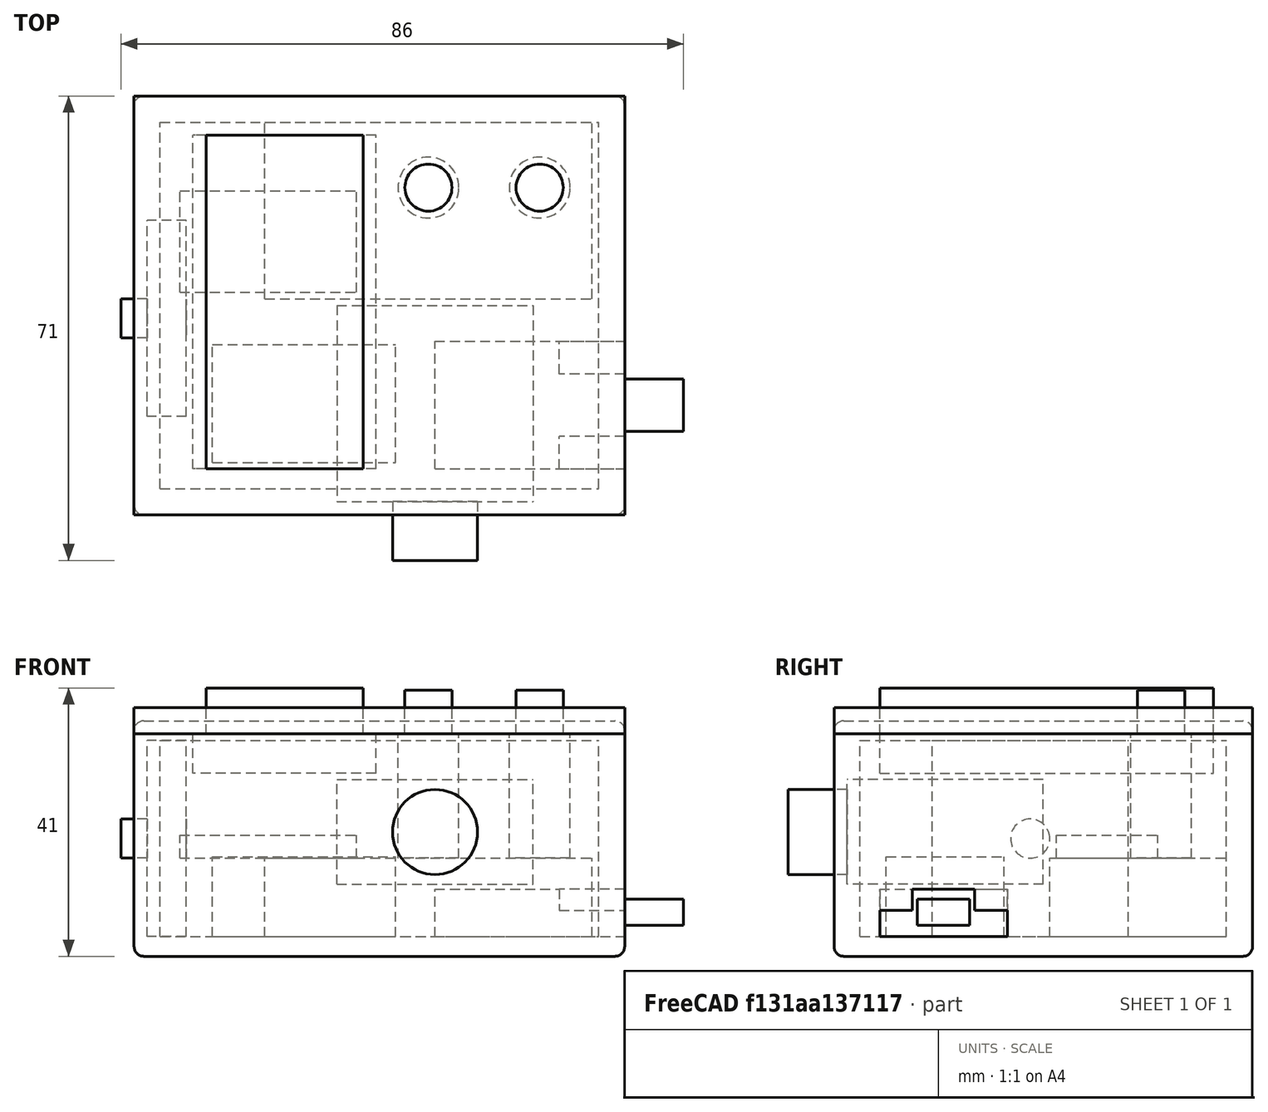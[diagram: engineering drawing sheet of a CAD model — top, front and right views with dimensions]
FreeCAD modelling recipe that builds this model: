
FCSTD DOCUMENT  (FreeCAD 0.19R)
Label: RoundTimer-partsonly
License: All rights reserved
LicenseURL: http://en.wikipedia.org/wiki/All_rights_reserved
objects: Part::Box×14, Part::Cylinder×6, Part::MultiFuse×4, Part::Fuse×2, Part::Cut×2, Part::Fillet×1
note: 29 computed .brp shape members not serialized (recipe doc carries the construction recipe); baked Part::Feature solids carry a one-line shape summary decoded from their .brp

FEATURE [Part::Box] Box  label="Cube"
  AttacherType = Attacher::AttachEngine3D
  Height = 30
  Length = 30
  Width = 16
FEATURE [Part::Cylinder] Cylinder
  Angle = 360
  AttacherType = Attacher::AttachEngine3D
  Height = 9
  Placement = pos=(15,8,30) rot=(0,0,1;0rad)
  Radius = 6.5
FEATURE [Part::Fuse] Fusion  label="Awesome switch"
  Base = -> Box
  Placement = pos=(-11,17,8) rot=(1,0,0;1.5708rad)
  Tool = -> Cylinder
FEATURE [Part::Box] Box001  label="Cube001"
  AttacherType = Attacher::AttachEngine3D
  Height = 6
  Length = 51
  Width = 28
FEATURE [Part::Box] Box002  label="Cube002"
  AttacherType = Attacher::AttachEngine3D
  Height = 7
  Length = 51
  Placement = pos=(0,2,6) rot=(0,0,1;0rad)
  Width = 24
FEATURE [Part::MultiFuse] Fusion001  label="LCD Display"
  Placement = pos=(-5,-8,25) rot=(0,0,1;1.5708rad)
  Shapes = -> [Box001,Box002]
FEATURE [Part::Box] Box003  label="Lipo Battery"
  AttacherType = Attacher::AttachEngine3D
  Height = 12
  Length = 50
  Placement = pos=(-22,18,0) rot=(0,0,1;0rad)
  Width = 27
FEATURE [Part::Cylinder] Cylinder001
  Angle = 360
  AttacherType = Attacher::AttachEngine3D
  Height = 19
  Radius = 4.65
FEATURE [Part::Cylinder] Cylinder002
  Angle = 360
  AttacherType = Attacher::AttachEngine3D
  Height = 6.7
  Placement = pos=(0,0,19) rot=(0,0,1;0rad)
  Radius = 3.6
FEATURE [Part::MultiFuse] Fusion002  label="Push Button mode/reset"
  Placement = pos=(20,35,12) rot=(1,0,0;0rad)
  Shapes = -> [Cylinder001,Cylinder002]
FEATURE [Part::Cylinder] Cylinder003
  Angle = 360
  AttacherType = Attacher::AttachEngine3D
  Height = 19
  Radius = 4.65
FEATURE [Part::Cylinder] Cylinder004
  Angle = 360
  AttacherType = Attacher::AttachEngine3D
  Height = 6.7
  Placement = pos=(0,0,19) rot=(0,0,1;0rad)
  Radius = 3.6
FEATURE [Part::MultiFuse] Fusion003  label="Push Button start/stop"
  Placement = pos=(3,35,12) rot=(1,0,0;0rad)
  Shapes = -> [Cylinder003,Cylinder004]
FEATURE [Part::Box] Box004  label="Cube003"
  AttacherType = Attacher::AttachEngine3D
  Height = 7.25
  Length = 29
  Width = 19.5
FEATURE [Part::Box] Box005  label="Cube004"
  AttacherType = Attacher::AttachEngine3D
  Height = 4
  Length = 10
  Placement = pos=(28,5.75,1.75) rot=(0,0,1;0rad)
  Width = 8
FEATURE [Part::Box] Box006  label="Cube005"
  AttacherType = Attacher::AttachEngine3D
  Height = 10
  Length = 10
  Placement = pos=(19,-5,4) rot=(0,0,1;0rad)
  Width = 10
FEATURE [Part::MultiFuse] Fusion004
  Shapes = -> [Box004,Box005]
FEATURE [Part::Cut] Cut
  Base = -> Fusion004
  Tool = -> Box006
FEATURE [Part::Box] Box007  label="Cube006"
  AttacherType = Attacher::AttachEngine3D
  Height = 10
  Length = 10
  Placement = pos=(19,14.5,4) rot=(0,0,1;0rad)
  Width = 10
FEATURE [Part::Cut] Cut001  label="USB Battery Charger"
  Base = -> Cut
  Placement = pos=(4,-8,0) rot=(0,0,1;0rad)
  Tool = -> Box007
FEATURE [Part::Box] Box008  label="Piezo Driver"
  AttacherType = Attacher::AttachEngine3D
  Height = 12.2
  Length = 28
  Placement = pos=(-30,-7,0) rot=(0,0,1;0rad)
  Width = 18
FEATURE [Part::Box] Box009  label="Cube007"
  AttacherType = Attacher::AttachEngine3D
  Height = 6
  Length = 30
  Width = 30
FEATURE [Part::Cylinder] Cylinder005
  Angle = 360
  AttacherType = Attacher::AttachEngine3D
  Height = 10
  Placement = pos=(15,15,0) rot=(0,0,1;0rad)
  Radius = 3
FEATURE [Part::Fuse] Fusion005  label="Piezo Buzzer"
  Base = -> Box009
  Placement = pos=(-34,0,0) rot=(0,-1,0;1.5708rad)
  Tool = -> Cylinder005
FEATURE [Part::Box] Box010  label="OuterBox"
  AttacherType = Attacher::AttachEngine3D
  Height = 36
  Length = 75
  Placement = pos=(-42,-15,-3) rot=(0,0,1;0rad)
  Width = 64
FEATURE [Part::Box] Box011  label="InnerBox"
  AttacherType = Attacher::AttachEngine3D
  Height = 30
  Length = 67
  Placement = pos=(-38,-11,0) rot=(0,0,1;0rad)
  Width = 56
FEATURE [Part::Box] Box012  label="LidRemove"
  AttacherType = Attacher::AttachEngine3D
  Height = 4
  Length = 75
  Placement = pos=(-42,-15,31) rot=(0,0,1;0rad)
  Width = 64
FEATURE [Part::Box] Box013  label="Arduino"
  AttacherType = Attacher::AttachEngine3D
  Height = 3.5
  Length = 27
  Placement = pos=(-35,19,12) rot=(0,0,1;0rad)
  Width = 15.5
FEATURE [Part::Fillet] Fillet
  Base = -> Box010
  Edges = 12 edges r=1.5: [Edge1,Edge2,Edge3,Edge4,Edge5,Edge6,Edge7,Edge8,Edge9,Edge10,Edge11,Edge12]
